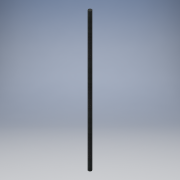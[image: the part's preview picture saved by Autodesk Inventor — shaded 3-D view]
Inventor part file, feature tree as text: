
AUTODESK INVENTOR PART (.ipt)
format: ipt  version: 2016 (Build 200138000, 138)  size: 93,184 bytes
history: native  units: in
note: dims shown in document units (in); Inventor stores cm internally (conversion verified against a paired STEP export)
features: extrude x1, sketch x1
ambient origin geometry x8: Origin, YZ Plane, XZ Plane, XY Plane, X Axis, Y Axis, Z Axis, Center Point
bodies: Solid1 (feature_tree)
feature tree (2):
  extrude  "Extrusion1"  Depth=22.0in TaperAngle=0.0deg
  sketch  "Sketch1"  dims[d0=0.5in d1=22.0in d2=0.0in]
